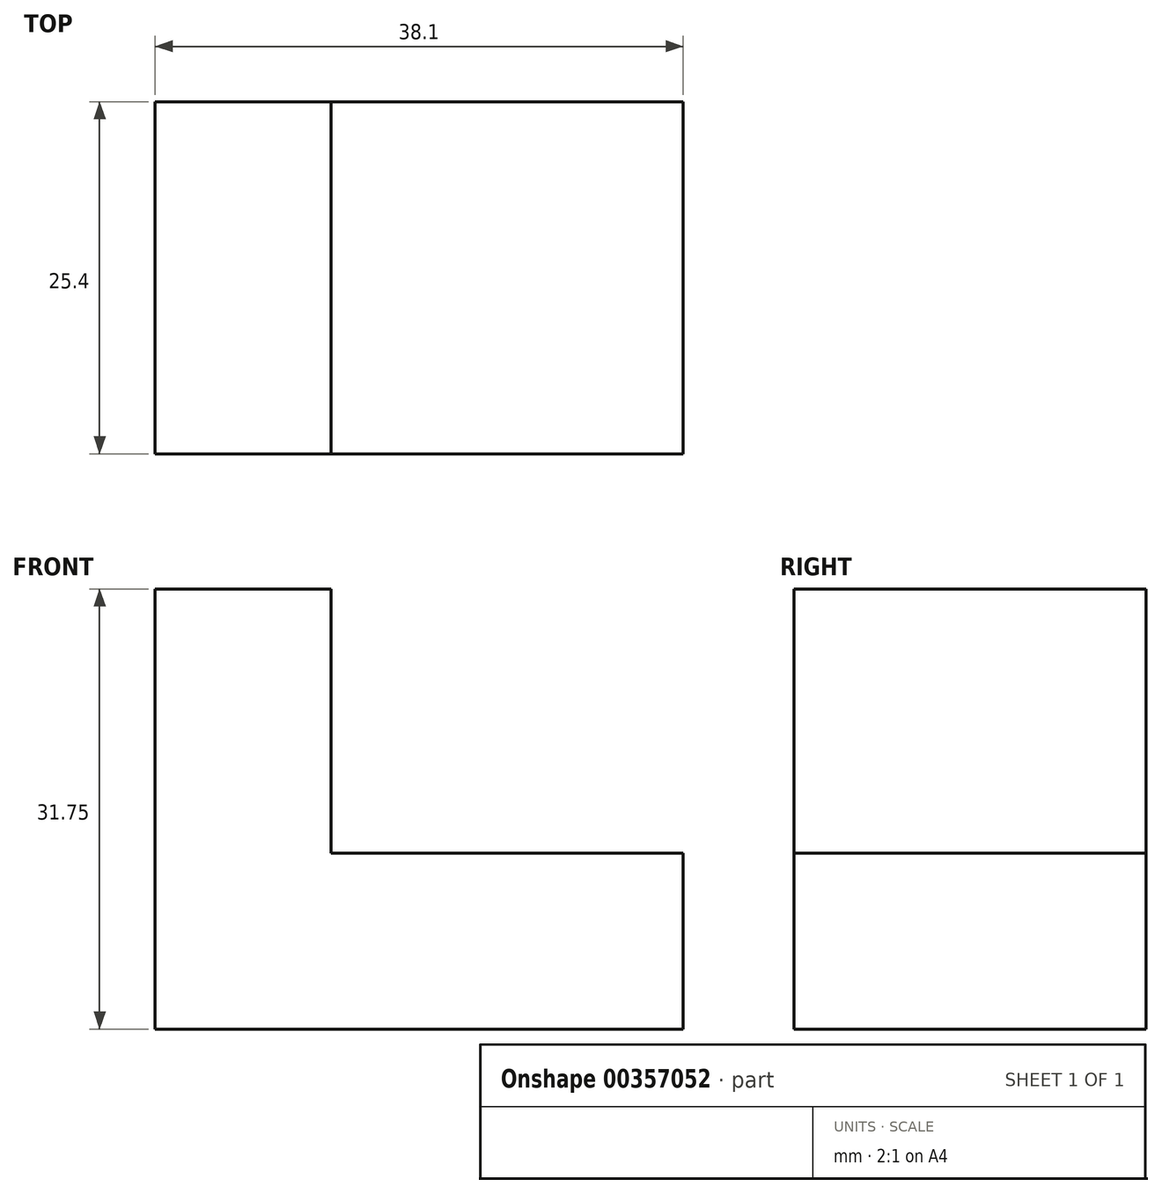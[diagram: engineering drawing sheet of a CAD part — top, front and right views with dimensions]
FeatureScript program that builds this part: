
annotation { "Feature Type Name" : "Feature", "Feature Type Description" : "" }
export const myFeature = defineFeature(function(context is Context, id is Id, definition is map)
    precondition{}
    {
        {
            var Q0;
            Q0=qCreatedBy(makeId("Front.planeOp"),FACE);
            var sketch = newSketch(context, id + "F0", { "sketchPlane" : qUnion([Q0])});
            skLineSegment(sketch, "E0", {"start": v(0, 0) * mm, "end": v(0, 31.75) * mm});
            skLineSegment(sketch, "E1", {"start": v(0, 31.75) * mm, "end": v(12.7, 31.75) * mm});
            skLineSegment(sketch, "E2", {"start": v(12.7, 31.75) * mm, "end": v(12.7, 12.7) * mm});
            skLineSegment(sketch, "E3", {"start": v(12.7, 12.7) * mm, "end": v(38.1, 12.7) * mm});
            skLineSegment(sketch, "E4", {"start": v(38.1, 12.7) * mm, "end": v(38.1, 0) * mm});
            skLineSegment(sketch, "E5", {"start": v(38.1, 0) * mm, "end": v(0, 0) * mm});
            skSolve(sketch);
        }
        {
            var Q0;
            Q0=qSketchRegion(id+"F0",true);
            extrude(context, id + "F1", {"entities" : qUnion([Q0]), "depth" : 25.4 * mm});
        }
    });
